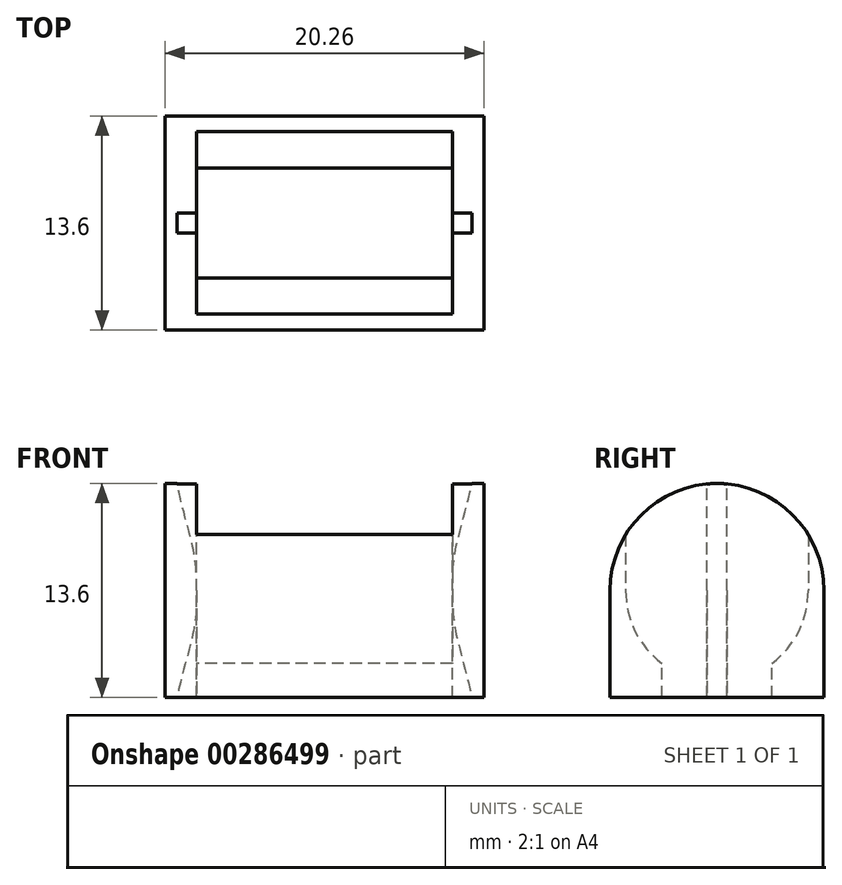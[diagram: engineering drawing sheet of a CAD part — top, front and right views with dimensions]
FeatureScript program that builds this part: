
annotation { "Feature Type Name" : "Feature", "Feature Type Description" : "" }
export const myFeature = defineFeature(function(context is Context, id is Id, definition is map)
    precondition{}
    {
        {
            var Q0;
            Q0=qCreatedBy(makeId("Front.planeOp"),FACE);
            var sketch = newSketch(context, id + "F0", { "sketchPlane" : qUnion([Q0])});
            skLineSegment(sketch, "E0.bottom", {"start": v(-8.12, 0) * mm, "end": v(8.12, 0) * mm});
            skLineSegment(sketch, "E0.top", {"start": v(-8.12, 5.8) * mm, "end": v(8.12, 5.8) * mm});
            skLineSegment(sketch, "E0.left", {"start": v(-8.12, 0) * mm, "end": v(-8.12, 5.8) * mm});
            skLineSegment(sketch, "E0.right", {"start": v(8.12, 0) * mm, "end": v(8.12, 5.8) * mm});
            skSolve(sketch);
        }
        {
            var Q0;
            Q0 = qSketchRegion(id + "F0", true);
            var Q1;
            Q1=sQuery(id+"F0.wireOp",EDGE,"E0.bottom");
            revolve(context, id + "F1", {"surfaceOperationType" : NewSurfaceOperationType.NEW, "entities" : qUnion([Q0]), "axis" : qUnion([Q1]), "revolveType" : RevolveType.FULL});
        }
        {
            var Q0;
            Q0=makeQuery(id+"F1.opRevolve","SWEPT_FACE",FACE,{"disambiguationData":[OSD([sQuery(id+"F0.wireOp",EDGE,"E0.left")])]});
            var sketch = newSketch(context, id + "F2", { "sketchPlane" : qUnion([Q0])});
            skLineSegment(sketch, "E1.bottom", {"start": v(6.8, -6.8) * mm, "end": v(-6.8, -6.8) * mm});
            skLineSegment(sketch, "E1.top", {"start": v(6.8, 6.8) * mm, "end": v(-6.8, 6.8) * mm});
            skLineSegment(sketch, "E1.left", {"start": v(6.8, -6.8) * mm, "end": v(6.8, 6.8) * mm});
            skLineSegment(sketch, "E1.right", {"start": v(-6.8, -6.8) * mm, "end": v(-6.8, 6.8) * mm});
            skPoint(sketch, "E1.middle", {"position": v(0, 0) * mm});
            skCircle(sketch, "E2.0.0", {"center": v(0, 0) * mm, "radius": 5.8 * mm});
            skLineSegment(sketch, "E3", {"start": v(-5.8, 0) * mm, "end": v(-5.8, 6.8) * mm});
            skLineSegment(sketch, "E4", {"start": v(5.8, 0) * mm, "end": v(5.8, 6.8) * mm});
            skArc(sketch, "E5", {"start": v(6.8, 0) * mm, "mid": v(0, 6.8) * mm, "end": v(-6.8, 0) * mm});
            skLineSegment(sketch, "E6", {"start": v(-3.5, -4.62) * mm, "end": v(-3.5, -6.8) * mm});
            skLineSegment(sketch, "E7.MirrorCS", {"start": v(3.5, -4.62) * mm, "end": v(3.5, -6.8) * mm});
            skSolve(sketch);
        }
        {
            var Q0;
            {var subQ0=sQuery(id+"F2.wireOp",EDGE,"E6");Q0=makeQuery(id+"F2.imprint","IMPRINT",FACE,{"disambiguationData":[TD([[makeQuery(id+"F2.imprint","IMPRINT",EDGE,{"derivedFrom":subQ0}),1.0]])]});}
            var Q1;
            {var subQ3=sQuery(id+"F2.wireOp",EDGE,"E7.MirrorCS");Q1=makeQuery(id+"F2.imprint","IMPRINT",FACE,{"disambiguationData":[TD([[makeQuery(id+"F2.imprint","IMPRINT",EDGE,{"derivedFrom":subQ3}),1.0]])]});}
            var Q2;
            {var subQ5=sQuery(id+"F2.wireOp",EDGE,"E6");Q2=makeQuery(id+"F2.imprint","IMPRINT",FACE,{"disambiguationData":[TD([[makeQuery(id+"F2.imprint","IMPRINT",EDGE,{"derivedFrom":subQ5}),-1.0]])]});}
            var Q3;
            {var subQ1=sQuery(id+"F2.wireOp",EDGE,"E2.0.0");var subQ6=sQuery(id+"F2.wireOp",EDGE,"E3");var subQ7=makeQuery(id+"F2.imprint","INTERSECT",VERTEX,{"derivedFrom":[subQ1,subQ6]});Q3=makeQuery(id+"F2.imprint","IMPRINT",FACE,{"disambiguationData":[TD([[makeQuery(id+"F2.imprint","IMPRINT",EDGE,{"disambiguationData":[TD([[subQ7,1.0]])],"derivedFrom":subQ1}),-1.0]])]});}
            var Q4;
            {var subQ0=sQuery(id+"F2.wireOp",EDGE,"E2.0.0");var subQ1=makeQuery(id+"F2.imprint","INTERSECT",VERTEX,{"derivedFrom":[subQ0,sQuery(id+"F2.wireOp",EDGE,"E3")]});Q4=makeQuery(id+"F2.imprint","IMPRINT",FACE,{"disambiguationData":[TD([[makeQuery(id+"F2.imprint","IMPRINT",EDGE,{"disambiguationData":[TD([[subQ1,-1.0]])],"derivedFrom":subQ0}),1.0]])]});}
            var Q5;
            Q5=makeQuery(id+"F1.opRevolve","SWEPT_FACE",FACE,{"disambiguationData":[OSD([sQuery(id+"F0.wireOp",EDGE,"E0.left")])]});
            var Q6;
            Q6=makeQuery(id+"FJT3lmwPM2Za0pN_1.opPattern","COPY",BODY,{"derivedFrom":makeQuery(id+"F1.opRevolve","SWEPT_BODY",BODY,{"disambiguationData":[OSD([sQuery(id+"F0.wireOp",EDGE,"E0.bottom"),sQuery(id+"F0.wireOp",EDGE,"E0.top"),sQuery(id+"F0.wireOp",EDGE,"E0.left"),sQuery(id+"F0.wireOp",EDGE,"E0.right")])]}),"instanceName":"1"});
            var Q7;
            Q7=makeQuery(id+"F1.opRevolve","SWEPT_FACE",FACE,{"disambiguationData":[OSD([sQuery(id+"F0.wireOp",EDGE,"E0.right")])]});
            extrude(context, id + "F3", {"entities" : qUnion([Q0, Q1, Q2, Q3, Q4]), "endBound" : BoundingType.UP_TO_SURFACE, "depth" : 25 * mm, "endBoundEntityFace" : qUnion([Q5]), "endBoundEntityBody" : qUnion([Q6]), "hasOffset" : true, "offsetDistance" : 2 * mm, "offsetOppositeDirection" : true, "hasSecondDirection" : true, "secondDirectionBound" : BoundingType.UP_TO_SURFACE, "secondDirectionOppositeDirection" : true, "secondDirectionDepth" : 2 * mm, "secondDirectionBoundEntityFace" : qUnion([Q7]), "hasSecondDirectionOffset" : true, "secondDirectionOffsetDistance" : 2 * mm, "secondDirectionOffsetOppositeDirection" : true});
        }
        {
            var Q0;
            {var subQ0=sQuery(id+"F2.wireOp",EDGE,"E2.0.0");var subQ1=makeQuery(id+"F2.imprint","INTERSECT",VERTEX,{"derivedFrom":[subQ0,sQuery(id+"F2.wireOp",EDGE,"E3")]});Q0=makeQuery(id+"F2.imprint","IMPRINT",FACE,{"disambiguationData":[TD([[makeQuery(id+"F2.imprint","IMPRINT",EDGE,{"disambiguationData":[TD([[subQ1,-1.0]])],"derivedFrom":subQ0}),1.0]])]});}
            var Q1;
            {var subQ1=sQuery(id+"F2.wireOp",EDGE,"E2.0.0");var subQ6=sQuery(id+"F2.wireOp",EDGE,"E3");var subQ7=makeQuery(id+"F2.imprint","INTERSECT",VERTEX,{"derivedFrom":[subQ1,subQ6]});Q1=makeQuery(id+"F2.imprint","IMPRINT",FACE,{"disambiguationData":[TD([[makeQuery(id+"F2.imprint","IMPRINT",EDGE,{"disambiguationData":[TD([[subQ7,1.0]])],"derivedFrom":subQ1}),-1.0]])]});}
            var Q2;
            {var subQ0=sQuery(id+"F2.wireOp",EDGE,"E6");Q2=makeQuery(id+"F2.imprint","IMPRINT",FACE,{"disambiguationData":[TD([[makeQuery(id+"F2.imprint","IMPRINT",EDGE,{"derivedFrom":subQ0}),1.0]])]});}
            var Q3;
            Q3=makeQuery(id+"F1.opRevolve","SWEPT_FACE",FACE,{"disambiguationData":[OSD([sQuery(id+"F0.wireOp",EDGE,"E0.right")])]});
            extrude(context, id + "F4", {"entities" : qUnion([Q0, Q1, Q2]), "operationType" : NewBodyOperationType.REMOVE, "endBound" : BoundingType.UP_TO_SURFACE, "oppositeDirection" : true, "depth" : 25 * mm, "endBoundEntityFace" : qUnion([Q3]), "offsetDistance" : 25 * mm});
        }
        {
            var Q0;
            Q0=qCreatedBy(makeId("Front.planeOp"),FACE);
            var sketch = newSketch(context, id + "F5", { "sketchPlane" : qUnion([Q0])});
            skLineSegment(sketch, "E8.0.0", {"start": v(-8.12, -6.8) * mm, "end": v(-8.12, -4.62) * mm});
            skLineSegment(sketch, "E8.0.1", {"start": v(-8.12, -4.62) * mm, "end": v(-8.12, 0) * mm});
            skLineSegment(sketch, "E8.0.2", {"start": v(-8.12, 0) * mm, "end": v(-8.12, 3.55) * mm});
            skLineSegment(sketch, "E8.0.3", {"start": v(-8.12, 3.55) * mm, "end": v(-8.12, 6.8) * mm});
            skLineSegment(sketch, "E8.0.4", {"start": v(-8.12, 3.55) * mm, "end": v(-8.12, 0) * mm});
            skLineSegment(sketch, "E8.0.5", {"start": v(-8.12, 0) * mm, "end": v(-8.12, -4.62) * mm});
            skLineSegment(sketch, "E8.0.6", {"start": v(-8.12, -4.62) * mm, "end": v(-8.12, -6.8) * mm});
            skFitSpline(sketch, "E9", {"points": [v(-8.12, 0) * mm, v(-9.38, 6.8) * mm], "startDerivative": vector(0, 8.22) * mm, "endDerivative": vector(-2.86, 12.18) * mm});
            skFitSpline(sketch, "E10.MirrorCS", {"points": [v(-8.12, 0) * mm, v(-9.38, -6.8) * mm], "startDerivative": vector(0, -8.22) * mm, "endDerivative": vector(-2.86, -12.18) * mm});
            skFitSpline(sketch, "E11.MirrorCS", {"points": [v(8.12, 0) * mm, v(9.38, 6.8) * mm], "startDerivative": vector(0, 8.22) * mm, "endDerivative": vector(2.86, 12.18) * mm});
            skFitSpline(sketch, "E12.MirrorCS", {"points": [v(8.12, 0) * mm, v(9.38, -6.8) * mm], "startDerivative": vector(0, -8.22) * mm, "endDerivative": vector(2.86, -12.18) * mm});
            skLineSegment(sketch, "E13", {"start": v(-9.38, 6.8) * mm, "end": v(9.38, 6.8) * mm});
            skLineSegment(sketch, "E14.0.0", {"start": v(8.12, -4.62) * mm, "end": v(8.12, 0) * mm});
            skLineSegment(sketch, "E14.0.1", {"start": v(8.12, -4.62) * mm, "end": v(8.12, -6.8) * mm});
            skLineSegment(sketch, "E14.0.3", {"start": v(8.12, -6.8) * mm, "end": v(8.12, -4.62) * mm});
            skLineSegment(sketch, "E14.0.4", {"start": v(8.12, 0) * mm, "end": v(8.12, -4.62) * mm});
            skLineSegment(sketch, "E14.0.5", {"start": v(8.12, 0) * mm, "end": v(8.12, 3.55) * mm});
            skLineSegment(sketch, "E14.0.6", {"start": v(8.12, 3.55) * mm, "end": v(8.12, 6.8) * mm});
            skLineSegment(sketch, "E14.0.7", {"start": v(8.12, 3.55) * mm, "end": v(8.12, 0) * mm});
            skLineSegment(sketch, "E15.0", {"start": v(-10.12, -6.8) * mm, "end": v(10.12, -6.8) * mm});
            skSolve(sketch);
        }
        {
            var Q0;
            Q0 = qSketchRegion(id + "F5", true);
            extrude(context, id + "F6", {"entities" : qUnion([Q0]), "operationType" : NewBodyOperationType.REMOVE, "oppositeDirection" : true, "depth" : 1.25 * mm, "offsetDistance" : 25 * mm, "symmetric" : true});
        }
    });
